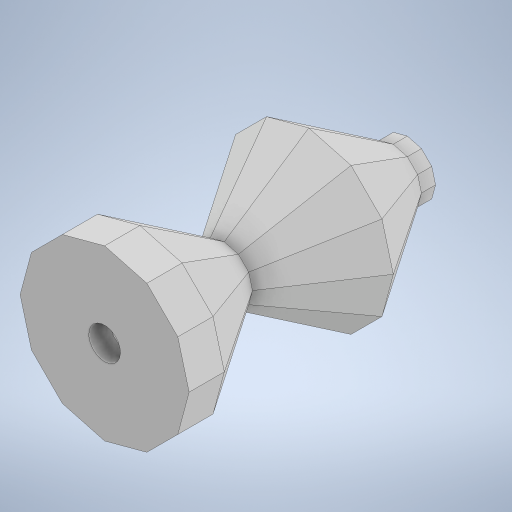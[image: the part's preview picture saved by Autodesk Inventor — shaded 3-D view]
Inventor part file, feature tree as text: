
AUTODESK INVENTOR PART (.ipt)
format: ipt  version: 2023 (Build 270158000, 158)  size: 352,768 bytes
history: native  units: in
note: dims shown in document units (in); Inventor stores cm internally (conversion verified against a paired STEP export)
features: sketch x6, extrude x4, projected_geometry x3, other x2, mirror x2, loft x1, shell x1
ambient origin geometry x8: Origin, YZ Plane, XZ Plane, XY Plane, X Axis, Y Axis, Z Axis, Center Point
bodies: Body1 (feature_tree)
feature tree (19):
  other  "솔리드1"
  sketch  "스케치1"
  other  "작업 평면1"
  loft  "로프트1"
  mirror  "미러1"
  mirror  "미러2"
  extrude  "돌출1"  Depth=0.4724in
  shell  "쉘1"  Thickness=0.315in
  extrude  "돌출2"  TaperAngle=0.0deg  [1 undecoded]
  extrude  "돌출3"  TaperAngle=0.0deg  [1 undecoded]
  extrude  "돌출4"  Depth=0.0984in TaperAngle=0.0deg
  sketch  "스케치2"
  sketch  "스케치3"
  projected_geometry  "투영된 루프1"
  sketch  "스케치4"
  projected_geometry  "투영된 루프2"
  sketch  "스케치5"
  sketch  "스케치6"
  projected_geometry  "투영된 루프3"
note: 2 required parameter values undecoded (feature->parameter linkage not recoverable at this tier; creation-order binding heuristic only, values carry confidence <= 0.55)
